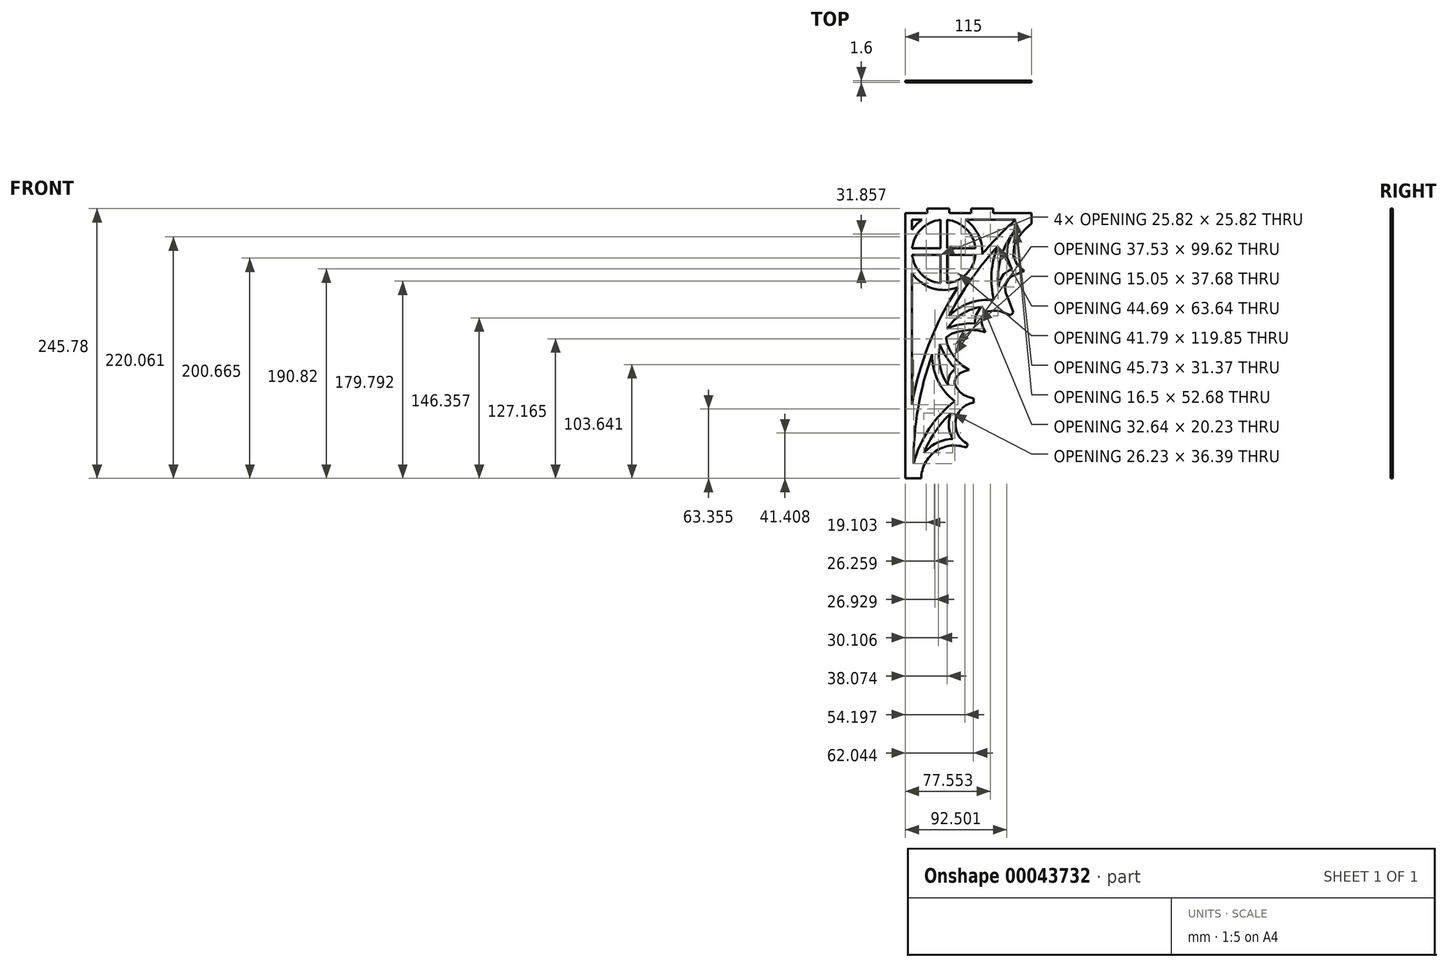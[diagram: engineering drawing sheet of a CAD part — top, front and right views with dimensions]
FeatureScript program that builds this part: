
annotation { "Feature Type Name" : "Feature", "Feature Type Description" : "" }
export const myFeature = defineFeature(function(context is Context, id is Id, definition is map)
    precondition{}
    {
        {
            var Q0;
            Q0=qCreatedBy(makeId("Front.planeOp"),FACE);
            var sketch = newSketch(context, id + "F0", { "sketchPlane" : qUnion([Q0])});
            skLineSegment(sketch, "E0", {"start": v(4.7, -50.11) * mm, "end": v(4.82, -53.73) * mm});
            skLineSegment(sketch, "E1", {"start": v(40.98, 28.4) * mm, "end": v(38.52, 25.73) * mm});
            skArc(sketch, "E2", {"start": v(-1.92, -94.86) * mm, "mid": v(-29.82, -98.07) * mm, "end": v(-42.98, -122.89) * mm});
            skLineSegment(sketch, "E3", {"start": v(-0.6, -91.48) * mm, "end": v(-1.92, -94.86) * mm});
            skArc(sketch, "E4", {"start": v(4.82, -53.73) * mm, "mid": v(-11.73, -70.62) * mm, "end": v(-0.6, -91.48) * mm});
            skLineSegment(sketch, "E5", {"start": v(38.52, 25.73) * mm, "end": v(29.3, 29.41) * mm});
            skLineSegment(sketch, "E6", {"start": v(29.3, 29.41) * mm, "end": v(23.88, 29.9) * mm});
            skLineSegment(sketch, "E7", {"start": v(23.88, 29.9) * mm, "end": v(17.75, 29.22) * mm});
            skLineSegment(sketch, "E8", {"start": v(17.75, 29.22) * mm, "end": v(14.94, 27.8) * mm});
            skLineSegment(sketch, "E9", {"start": v(14.94, 27.8) * mm, "end": v(13.7, 25.74) * mm});
            skLineSegment(sketch, "E10", {"start": v(13.7, 25.74) * mm, "end": v(12.47, 23.68) * mm});
            skLineSegment(sketch, "E11", {"start": v(12.47, 23.68) * mm, "end": v(12.19, 21.13) * mm});
            skLineSegment(sketch, "E12", {"start": v(12.19, 21.13) * mm, "end": v(11.9, 18.57) * mm});
            skLineSegment(sketch, "E13", {"start": v(11.9, 18.57) * mm, "end": v(12.66, 16.43) * mm});
            skLineSegment(sketch, "E14", {"start": v(12.66, 16.43) * mm, "end": v(13.4, 14.3) * mm});
            skLineSegment(sketch, "E15", {"start": v(13.4, 14.3) * mm, "end": v(15.46, 10.35) * mm});
            skLineSegment(sketch, "E16", {"start": v(4.7, -50.11) * mm, "end": v(-0.6, -48.59) * mm});
            skLineSegment(sketch, "E17", {"start": v(-0.6, -48.59) * mm, "end": v(-4.89, -46.48) * mm});
            skLineSegment(sketch, "E18", {"start": v(-4.89, -46.48) * mm, "end": v(-8.14, -43.54) * mm});
            skLineSegment(sketch, "E19", {"start": v(-8.14, -43.54) * mm, "end": v(-11.81, -38.59) * mm});
            skLineSegment(sketch, "E20", {"start": v(-11.81, -38.59) * mm, "end": v(-12.69, -35.56) * mm});
            skLineSegment(sketch, "E21", {"start": v(-12.69, -35.56) * mm, "end": v(-12.02, -33.26) * mm});
            skLineSegment(sketch, "E22", {"start": v(-12.02, -33.26) * mm, "end": v(-11.35, -30.96) * mm});
            skLineSegment(sketch, "E23", {"start": v(-11.35, -30.96) * mm, "end": v(-9.67, -29) * mm});
            skLineSegment(sketch, "E24", {"start": v(-9.67, -29) * mm, "end": v(-7.99, -27.06) * mm});
            skLineSegment(sketch, "E25", {"start": v(-7.99, -27.06) * mm, "end": v(-5.91, -26.16) * mm});
            skLineSegment(sketch, "E26", {"start": v(-5.91, -26.16) * mm, "end": v(-3.84, -25.25) * mm});
            skLineSegment(sketch, "E27", {"start": v(-3.84, -25.25) * mm, "end": v(0.45, -24.07) * mm});
            skLineSegment(sketch, "E28", {"start": v(15.46, 10.35) * mm, "end": v(8.74, 12) * mm});
            skLineSegment(sketch, "E29", {"start": v(8.74, 12) * mm, "end": v(0.92, 12.48) * mm});
            skLineSegment(sketch, "E30", {"start": v(0.92, 12.48) * mm, "end": v(-8.8, 11.07) * mm});
            skLineSegment(sketch, "E31", {"start": v(-8.8, 11.07) * mm, "end": v(-15.35, 8.95) * mm});
            skLineSegment(sketch, "E32", {"start": v(-15.35, 8.95) * mm, "end": v(-20.43, 5.52) * mm});
            skLineSegment(sketch, "E33", {"start": v(0.45, -24.07) * mm, "end": v(-5.33, -20.28) * mm});
            skLineSegment(sketch, "E34", {"start": v(-5.33, -20.28) * mm, "end": v(-11, -14.87) * mm});
            skLineSegment(sketch, "E35", {"start": v(-11, -14.87) * mm, "end": v(-16.58, -6.8) * mm});
            skLineSegment(sketch, "E36", {"start": v(-16.58, -6.8) * mm, "end": v(-19.5, -0.54) * mm});
            skLineSegment(sketch, "E37", {"start": v(-19.5, -0.54) * mm, "end": v(-20.43, 5.52) * mm});
            skLineSegment(sketch, "E38", {"start": v(40.98, 28.4) * mm, "end": v(36.36, 40.16) * mm});
            skLineSegment(sketch, "E39", {"start": v(36.36, 40.16) * mm, "end": v(34.07, 46.17) * mm});
            skLineSegment(sketch, "E40", {"start": v(34.07, 46.17) * mm, "end": v(33.57, 48.95) * mm});
            skLineSegment(sketch, "E41", {"start": v(33.57, 48.95) * mm, "end": v(33.26, 51.14) * mm});
            skLineSegment(sketch, "E42", {"start": v(33.26, 51.14) * mm, "end": v(34.1, 55.06) * mm});
            skLineSegment(sketch, "E43", {"start": v(34.1, 55.06) * mm, "end": v(36.63, 59) * mm});
            skLineSegment(sketch, "E44", {"start": v(36.63, 59) * mm, "end": v(39.75, 61.35) * mm});
            skLineSegment(sketch, "E45", {"start": v(39.75, 61.35) * mm, "end": v(50.72, 66.32) * mm});
            skLineSegment(sketch, "E46", {"start": v(57.5, 109.5) * mm, "end": v(52.27, 104.95) * mm});
            skLineSegment(sketch, "E47", {"start": v(52.27, 104.95) * mm, "end": v(48.12, 100.52) * mm});
            skLineSegment(sketch, "E48", {"start": v(48.12, 100.52) * mm, "end": v(43.8, 93.76) * mm});
            skLineSegment(sketch, "E49", {"start": v(43.8, 93.76) * mm, "end": v(41.52, 88.13) * mm});
            skLineSegment(sketch, "E50", {"start": v(41.52, 88.13) * mm, "end": v(41.08, 80.23) * mm});
            skLineSegment(sketch, "E51", {"start": v(41.08, 80.23) * mm, "end": v(44.08, 72.3) * mm});
            skLineSegment(sketch, "E52", {"start": v(44.08, 72.3) * mm, "end": v(50.72, 66.32) * mm});
            skArc(sketch, "E53", {"start": v(-32.98, -9.72) * mm, "mid": v(-45.89, -58.78) * mm, "end": v(-50, -109.35) * mm});
            skArc(sketch, "E54", {"start": v(-15.9, -63.29) * mm, "mid": v(-17.9, -75.25) * mm, "end": v(-14.28, -86.82) * mm});
            skArc(sketch, "E55", {"start": v(-14.28, -86.82) * mm, "mid": v(-28.75, -90.48) * mm, "end": v(-40.5, -99.68) * mm});
            skArc(sketch, "E56", {"start": v(-32.98, -9.72) * mm, "mid": v(-27.95, -33.58) * mm, "end": v(-12.47, -52.41) * mm});
            skArc(sketch, "E57", {"start": v(-25.62, -0.4) * mm, "mid": v(-26.12, -20.07) * mm, "end": v(-18.24, -38.1) * mm});
            skArc(sketch, "E58", {"start": v(-12.47, -52.41) * mm, "mid": v(-35.92, -77.8) * mm, "end": v(-50, -109.35) * mm});
            skArc(sketch, "E59", {"start": v(-15.9, -63.29) * mm, "mid": v(-30.21, -80.12) * mm, "end": v(-40.5, -99.68) * mm});
            skArc(sketch, "E60", {"start": v(26.89, 88.72) * mm, "mid": v(2.4, 58.41) * mm, "end": v(-17.8, 25.08) * mm});
            skArc(sketch, "E61", {"start": v(23.29, 39.68) * mm, "mid": v(1.12, 36.97) * mm, "end": v(-17.8, 25.08) * mm});
            skLineSegment(sketch, "E62", {"start": v(-11.9, -22.35) * mm, "end": v(-15.62, -18.8) * mm});
            skLineSegment(sketch, "E63", {"start": v(-15.62, -18.8) * mm, "end": v(-21.84, -9.8) * mm});
            skLineSegment(sketch, "E64", {"start": v(-21.84, -9.8) * mm, "end": v(-25.33, -2.31) * mm});
            skLineSegment(sketch, "E65", {"start": v(-25.33, -2.31) * mm, "end": v(-25.62, -0.4) * mm});
            skLineSegment(sketch, "E66", {"start": v(-18.24, -38.1) * mm, "end": v(-18.97, -35.55) * mm});
            skLineSegment(sketch, "E67", {"start": v(-18.97, -35.55) * mm, "end": v(-17.82, -31.58) * mm});
            skLineSegment(sketch, "E68", {"start": v(-17.82, -31.58) * mm, "end": v(-16.78, -28.01) * mm});
            skLineSegment(sketch, "E69", {"start": v(-16.78, -28.01) * mm, "end": v(-14.24, -25.06) * mm});
            skLineSegment(sketch, "E70", {"start": v(-14.24, -25.06) * mm, "end": v(-11.9, -22.35) * mm});
            skLineSegment(sketch, "E71", {"start": v(5.8, 18.23) * mm, "end": v(0.67, 18.54) * mm});
            skLineSegment(sketch, "E72", {"start": v(0.67, 18.54) * mm, "end": v(-10.16, 16.97) * mm});
            skLineSegment(sketch, "E73", {"start": v(-10.16, 16.97) * mm, "end": v(-18.03, 14.43) * mm});
            skLineSegment(sketch, "E74", {"start": v(-18.03, 14.43) * mm, "end": v(-19.62, 13.35) * mm});
            skArc(sketch, "E75", {"start": v(13.02, 33.58) * mm, "mid": v(-5.55, 27.1) * mm, "end": v(-19.62, 13.35) * mm});
            skLineSegment(sketch, "E76", {"start": v(13.02, 33.58) * mm, "end": v(10.66, 32.4) * mm});
            skLineSegment(sketch, "E77", {"start": v(10.66, 32.4) * mm, "end": v(8.53, 28.84) * mm});
            skLineSegment(sketch, "E78", {"start": v(8.53, 28.84) * mm, "end": v(6.62, 25.66) * mm});
            skLineSegment(sketch, "E79", {"start": v(6.62, 25.66) * mm, "end": v(6.2, 21.79) * mm});
            skLineSegment(sketch, "E80", {"start": v(6.2, 21.79) * mm, "end": v(5.8, 18.23) * mm});
            skArc(sketch, "E81", {"start": v(26.89, 88.72) * mm, "mid": v(21.01, 64.5) * mm, "end": v(23.29, 39.68) * mm});
            skLineSegment(sketch, "E82", {"start": v(27.15, 51.44) * mm, "end": v(28.44, 57.4) * mm});
            skLineSegment(sketch, "E83", {"start": v(28.44, 57.4) * mm, "end": v(32.14, 63.16) * mm});
            skLineSegment(sketch, "E84", {"start": v(32.14, 63.16) * mm, "end": v(36.65, 66.57) * mm});
            skLineSegment(sketch, "E85", {"start": v(36.65, 66.57) * mm, "end": v(39.83, 68) * mm});
            skLineSegment(sketch, "E86", {"start": v(43.25, 104.11) * mm, "end": v(38.41, 96.54) * mm});
            skLineSegment(sketch, "E87", {"start": v(38.41, 96.54) * mm, "end": v(35.55, 89.47) * mm});
            skLineSegment(sketch, "E88", {"start": v(35.55, 89.47) * mm, "end": v(34.98, 79.3) * mm});
            skLineSegment(sketch, "E89", {"start": v(34.98, 79.3) * mm, "end": v(38.96, 68.8) * mm});
            skLineSegment(sketch, "E90", {"start": v(38.96, 68.8) * mm, "end": v(39.83, 68) * mm});
            skArc(sketch, "E91", {"start": v(43.25, 104.11) * mm, "mid": v(29.81, 79.42) * mm, "end": v(27.15, 51.44) * mm});
            skLineSegment(sketch, "E92", {"start": v(-42.98, -122.89) * mm, "end": v(-57.5, -122.89) * mm});
            skLineSegment(sketch, "E93", {"start": v(57.5, 118.89) * mm, "end": v(22.5, 118.89) * mm});
            skLineSegment(sketch, "E94", {"start": v(57.5, 109.5) * mm, "end": v(57.5, 118.89) * mm});
            skLineSegment(sketch, "E95", {"start": v(-57.5, -122.89) * mm, "end": v(-57.5, 118.89) * mm});
            skArc(sketch, "E96", {"start": v(12.48, 81.49) * mm, "mid": v(9.02, 99.21) * mm, "end": v(-2.81, 112.85) * mm});
            skArc(sketch, "E97", {"start": v(-9.68, 51.25) * mm, "mid": v(-35.83, -0.15) * mm, "end": v(-51.47, -55.65) * mm});
            skLineSegment(sketch, "E98", {"start": v(-42.13, 112.85) * mm, "end": v(-51.47, 112.85) * mm});
            skArc(sketch, "E99", {"start": v(42.92, 112.85) * mm, "mid": v(27.12, 97.74) * mm, "end": v(12.48, 81.49) * mm});
            skLineSegment(sketch, "E100", {"start": v(-51.47, 103.51) * mm, "end": v(-51.47, 112.85) * mm});
            skLineSegment(sketch, "E101", {"start": v(42.92, 112.85) * mm, "end": v(-2.81, 112.85) * mm});
            skArc(sketch, "E102", {"start": v(-51.47, 64.2) * mm, "mid": v(-32.84, 50.4) * mm, "end": v(-9.68, 51.25) * mm});
            skLineSegment(sketch, "E103", {"start": v(-51.47, -55.65) * mm, "end": v(-51.47, 64.2) * mm});
            skArc(sketch, "E104", {"start": v(-42.13, 112.85) * mm, "mid": v(-47.24, 108.63) * mm, "end": v(-51.47, 103.51) * mm});
            skLineSegment(sketch, "E105", {"start": v(-51.3, 86.88) * mm, "end": v(-25.49, 86.88) * mm});
            skLineSegment(sketch, "E106", {"start": v(-51.3, 80.84) * mm, "end": v(-25.49, 80.84) * mm});
            skArc(sketch, "E107", {"start": v(-19.45, 55.02) * mm, "mid": v(-1.96, 63.35) * mm, "end": v(6.37, 80.84) * mm});
            skArc(sketch, "E108", {"start": v(-25.49, 112.7) * mm, "mid": v(-42.97, 104.36) * mm, "end": v(-51.3, 86.88) * mm});
            skArc(sketch, "E109", {"start": v(-51.3, 80.84) * mm, "mid": v(-42.97, 63.35) * mm, "end": v(-25.49, 55.02) * mm});
            skLineSegment(sketch, "E110", {"start": v(-25.49, 112.7) * mm, "end": v(-25.49, 86.88) * mm});
            skLineSegment(sketch, "E111", {"start": v(-19.45, 80.84) * mm, "end": v(6.37, 80.84) * mm});
            skLineSegment(sketch, "E112", {"start": v(-19.45, 112.7) * mm, "end": v(-19.45, 86.88) * mm});
            skArc(sketch, "E113", {"start": v(6.37, 86.88) * mm, "mid": v(-1.96, 104.36) * mm, "end": v(-19.45, 112.7) * mm});
            skLineSegment(sketch, "E114", {"start": v(-19.45, 80.84) * mm, "end": v(-19.45, 55.02) * mm});
            skLineSegment(sketch, "E115", {"start": v(-19.45, 86.88) * mm, "end": v(6.37, 86.88) * mm});
            skLineSegment(sketch, "E116", {"start": v(-25.49, 80.84) * mm, "end": v(-25.49, 55.02) * mm});
            skLineSegment(sketch, "E117", {"start": v(-37.5, 122.89) * mm, "end": v(-37.5, 118.89) * mm});
            skLineSegment(sketch, "E118", {"start": v(-17.5, 122.89) * mm, "end": v(-17.5, 118.89) * mm});
            skLineSegment(sketch, "E119", {"start": v(22.5, 122.89) * mm, "end": v(22.5, 118.89) * mm});
            skLineSegment(sketch, "E120", {"start": v(22.5, 122.89) * mm, "end": v(2.5, 122.89) * mm});
            skLineSegment(sketch, "E121", {"start": v(2.5, 122.89) * mm, "end": v(2.5, 118.89) * mm});
            skLineSegment(sketch, "E122", {"start": v(-37.5, 118.89) * mm, "end": v(-57.5, 118.89) * mm});
            skLineSegment(sketch, "E123", {"start": v(2.5, 118.89) * mm, "end": v(-17.5, 118.89) * mm});
            skLineSegment(sketch, "E124", {"start": v(-17.5, 122.89) * mm, "end": v(-37.5, 122.89) * mm});
            skSolve(sketch);
        }
        {
            var Q0;
            Q0=makeQuery(id+"F0.imprint","IMPRINT",FACE,{"disambiguationData":[TD([[makeQuery(id+"F0.imprint","IMPRINT",EDGE,{"derivedFrom":sQuery(id+"F0.wireOp",EDGE,"E0")}),-1.0]])]});
            extrude(context, id + "F1", {"entities" : qUnion([Q0]), "depth" : 1.6 * mm});
        }
        {
            var Q0;
            Q0=makeQuery(id+"F1.opExtrude","SWEPT_FACE",FACE,{"disambiguationData":[OSD([sQuery(id+"F0.wireOp",EDGE,"E122")])]});
            var sketch = newSketch(context, id + "F2", { "sketchPlane" : qUnion([Q0])});
            skLineSegment(sketch, "E125", {"start": v(-57.5, -0.8) * mm, "end": v(-81.65, -0.8) * mm, "construction": true});
            skSolve(sketch);
        }
    });
